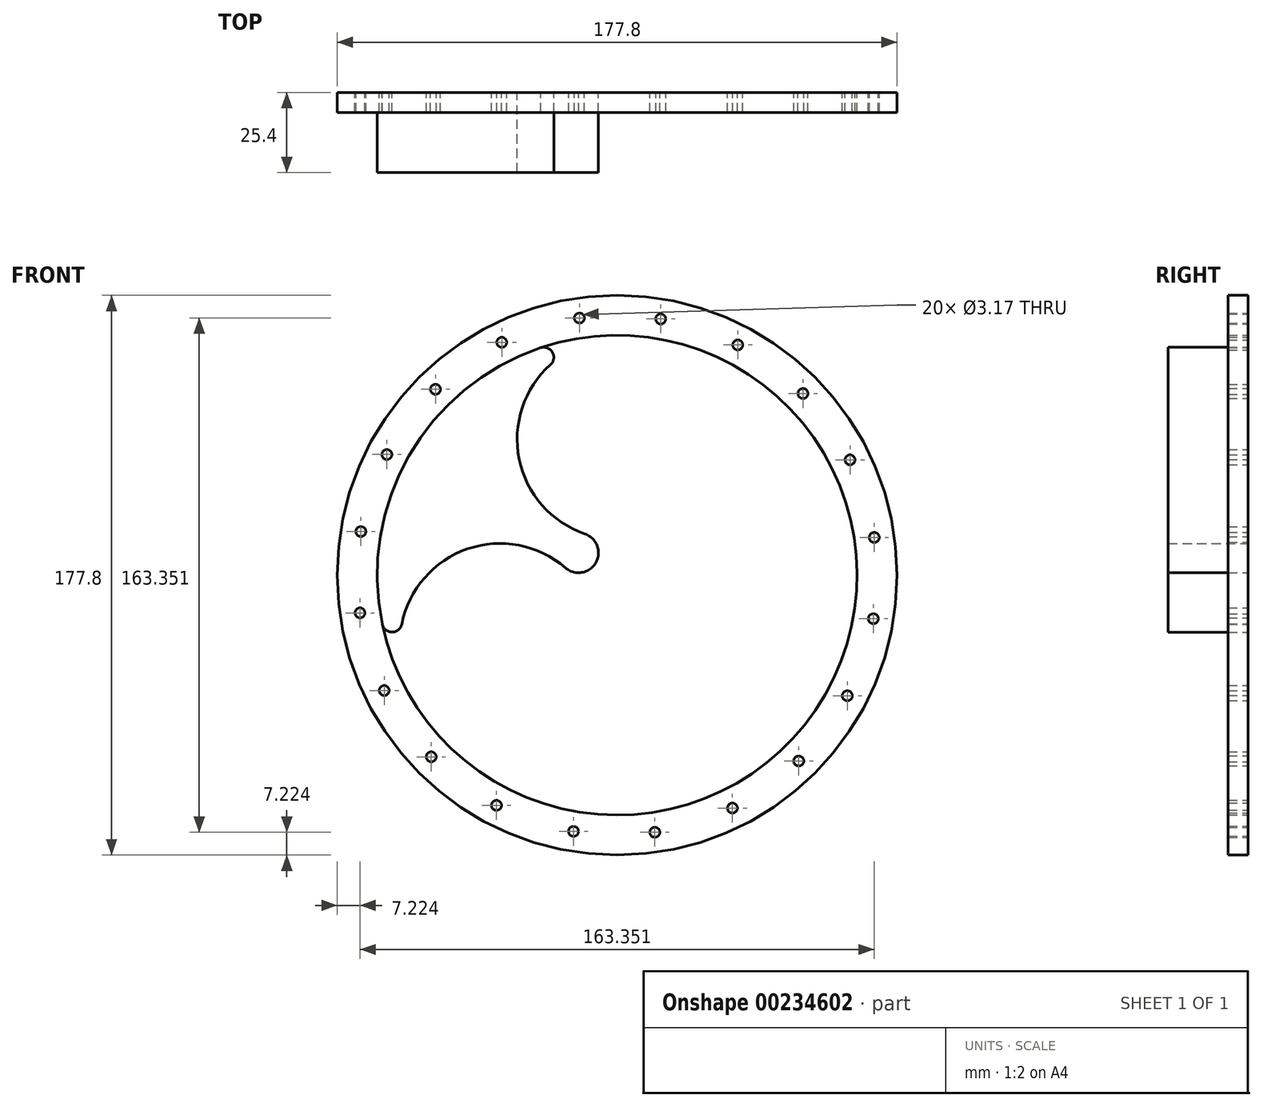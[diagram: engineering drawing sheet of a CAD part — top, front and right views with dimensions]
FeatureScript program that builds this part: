
annotation { "Feature Type Name" : "Feature", "Feature Type Description" : "" }
export const myFeature = defineFeature(function(context is Context, id is Id, definition is map)
    precondition{}
    {
        {
            var Q0;
            Q0=qCreatedBy(makeId("Front.planeOp"),FACE);
            var sketch = newSketch(context, id + "F0", { "sketchPlane" : qUnion([Q0])});
            skCircle(sketch, "E0", {"center": v(0, 0) * mm, "radius": 82.55 * mm, "construction": true});
            skCircle(sketch, "E1", {"center": v(13.84, 81.38) * mm, "radius": 1.59 * mm});
            skCircle(sketch, "E2.1.0", {"center": v(-11.98, 81.68) * mm, "radius": 1.59 * mm});
            skCircle(sketch, "E2.2.0", {"center": v(-36.64, 73.97) * mm, "radius": 1.59 * mm});
            skCircle(sketch, "E3.1.3.0", {"center": v(-57.7, 59.03) * mm, "radius": 1.59 * mm});
            skCircle(sketch, "E3.1.4.0", {"center": v(-73.12, 38.31) * mm, "radius": 1.59 * mm});
            skCircle(sketch, "E3.1.5.0", {"center": v(-81.38, 13.84) * mm, "radius": 1.59 * mm});
            skCircle(sketch, "E3.1.6.0", {"center": v(-81.68, -11.98) * mm, "radius": 1.59 * mm});
            skCircle(sketch, "E3.1.7.0", {"center": v(-73.97, -36.64) * mm, "radius": 1.59 * mm});
            skCircle(sketch, "E3.1.8.0", {"center": v(-59.03, -57.7) * mm, "radius": 1.59 * mm});
            skCircle(sketch, "E3.1.9.0", {"center": v(-38.31, -73.12) * mm, "radius": 1.59 * mm});
            skCircle(sketch, "E3.1.10.0", {"center": v(-13.84, -81.38) * mm, "radius": 1.59 * mm});
            skCircle(sketch, "E3.1.11.0", {"center": v(11.98, -81.68) * mm, "radius": 1.59 * mm});
            skCircle(sketch, "E3.1.12.0", {"center": v(36.64, -73.97) * mm, "radius": 1.59 * mm});
            skCircle(sketch, "E3.1.13.0", {"center": v(57.7, -59.03) * mm, "radius": 1.59 * mm});
            skCircle(sketch, "E3.1.14.0", {"center": v(73.12, -38.31) * mm, "radius": 1.59 * mm});
            skCircle(sketch, "E3.1.15.0", {"center": v(81.38, -13.84) * mm, "radius": 1.59 * mm});
            skCircle(sketch, "E3.1.16.0", {"center": v(81.68, 11.98) * mm, "radius": 1.59 * mm});
            skCircle(sketch, "E3.1.17.0", {"center": v(73.97, 36.64) * mm, "radius": 1.59 * mm});
            skCircle(sketch, "E3.1.18.0", {"center": v(59.03, 57.7) * mm, "radius": 1.59 * mm});
            skCircle(sketch, "E3.1.19.0", {"center": v(38.31, 73.12) * mm, "radius": 1.59 * mm});
            skCircle(sketch, "E4", {"center": v(0, 0) * mm, "radius": 88.9 * mm});
            skCircle(sketch, "E5", {"center": v(0, 0) * mm, "radius": 76.2 * mm});
            skCircle(sketch, "E6", {"center": v(0, 43.18) * mm, "radius": 31.75 * mm});
            skCircle(sketch, "E7.1.0", {"center": v(-37.22, -21.69) * mm, "radius": 31.75 * mm});
            skCircle(sketch, "E7.2.0", {"center": v(37.57, -21.5) * mm, "radius": 31.75 * mm});
            skPoint(sketch, "E7.center", {"position": v(0.11, 0) * mm});
            skArc(sketch, "E8", {"start": v(-11.4, 0.83) * mm, "mid": v(9.9, -5.73) * mm, "end": v(-6.4, 9.48) * mm});
            skArc(sketch, "E9", {"start": v(-21.16, 66.85) * mm, "mid": v(-20.54, 70.81) * mm, "end": v(-24.3, 72.22) * mm});
            skArc(sketch, "E10", {"start": v(-74.6, -15.56) * mm, "mid": v(-71.47, -18.09) * mm, "end": v(-68.37, -15.53) * mm});
            skArc(sketch, "E11", {"start": v(-16.44, 2.31) * mm, "mid": v(-6.78, 3.95) * mm, "end": v(-10.24, 13.13) * mm});
            skSolve(sketch);
        }
        {
            var Q0;
            {var subQ0=sQuery(id+"F0.wireOp",EDGE,"E9");Q0=makeQuery(id+"F0.imprint","IMPRINT",FACE,{"disambiguationData":[TD([[makeQuery(id+"F0.imprint","IMPRINT",EDGE,{"derivedFrom":subQ0}),1.0]])]});}
            var Q1;
            Q1=makeQuery(id+"F0.imprint","IMPRINT",FACE,{"disambiguationData":[TD([[makeQuery(id+"F0.imprint","IMPRINT",EDGE,{"derivedFrom":sQuery(id+"F0.wireOp",EDGE,"E1")}),-1.0]])]});
            extrude(context, id + "F1", {"entities" : qUnion([Q0, Q1]), "depth" : 6.35 * mm, "offsetDistance" : 25.4 * mm});
        }
        {
            var Q0;
            {var subQ0=sQuery(id+"F0.wireOp",EDGE,"E9");Q0=makeQuery(id+"F0.imprint","IMPRINT",FACE,{"disambiguationData":[TD([[makeQuery(id+"F0.imprint","IMPRINT",EDGE,{"derivedFrom":subQ0}),1.0]])]});}
            extrude(context, id + "F2", {"entities" : qUnion([Q0]), "operationType" : NewBodyOperationType.ADD, "depth" : 25.4 * mm, "offsetDistance" : 25.4 * mm});
        }
    });
